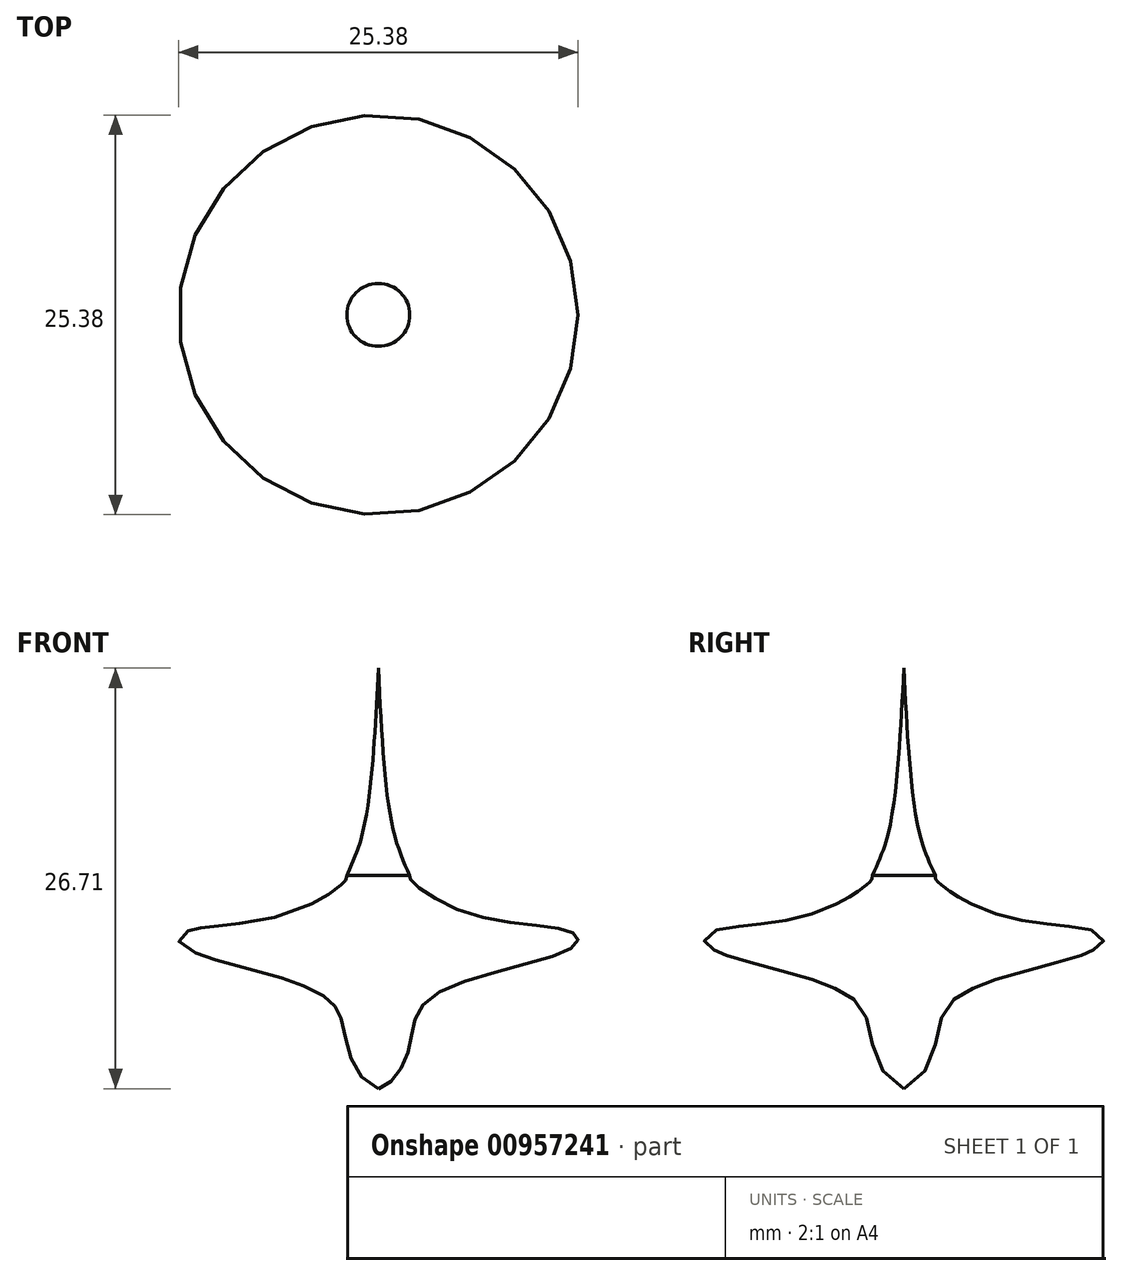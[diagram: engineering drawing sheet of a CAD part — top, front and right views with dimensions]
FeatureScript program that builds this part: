
annotation { "Feature Type Name" : "Feature", "Feature Type Description" : "" }
export const myFeature = defineFeature(function(context is Context, id is Id, definition is map)
    precondition{}
    {
        {
            var Q0;
            Q0=qCreatedBy(makeId("Front.planeOp"),FACE);
            var sketch = newSketch(context, id + "F0", { "sketchPlane" : qUnion([Q0])});
            skLineSegment(sketch, "E0", {"start": v(0, 9.84) * mm, "end": v(0, -11.63) * mm});
            skFitSpline(sketch, "E1", {"points": [v(0, -11.63) * mm, v(1.93, -9.12) * mm, v(3.35, -5.83) * mm, v(12.32, -2.66) * mm, v(12.52, -1.82) * mm, v(6.06, -0.6) * mm, v(2, 1.72) * mm, v(2, 1.92) * mm], "startDerivative": vector(19.94, 5.35) * mm, "endDerivative": vector(1.78, 4.54) * mm});
            skFitSpline(sketch, "E2", {"points": [v(2, 1.92) * mm, v(0.9, 5.02) * mm, v(0, 15.08) * mm], "startDerivative": vector(-3.31, 7.2) * mm, "endDerivative": vector(-0.9, 18.12) * mm});
            skLineSegment(sketch, "E3", {"start": v(0, 9.84) * mm, "end": v(0, 15.08) * mm});
            skLineSegment(sketch, "E4", {"start": v(-21.56, 0.98) * mm, "end": v(-21.56, 1.01) * mm});
            skSolve(sketch);
        }
        {
            var Q0;
            Q0=makeQuery(id+"F0.imprint","IMPRINT",FACE,{"disambiguationData":[TD([[makeQuery(id+"F0.imprint","IMPRINT",EDGE,{"derivedFrom":sQuery(id+"F0.wireOp",EDGE,"E0")}),1.0]])]});
            var Q1;
            Q1=sQuery(id+"F0.wireOp",EDGE,"E0");
            revolve(context, id + "F1", {"surfaceOperationType" : NewSurfaceOperationType.NEW, "entities" : qUnion([Q0]), "axis" : qUnion([Q1]), "revolveType" : RevolveType.FULL});
        }
    });
